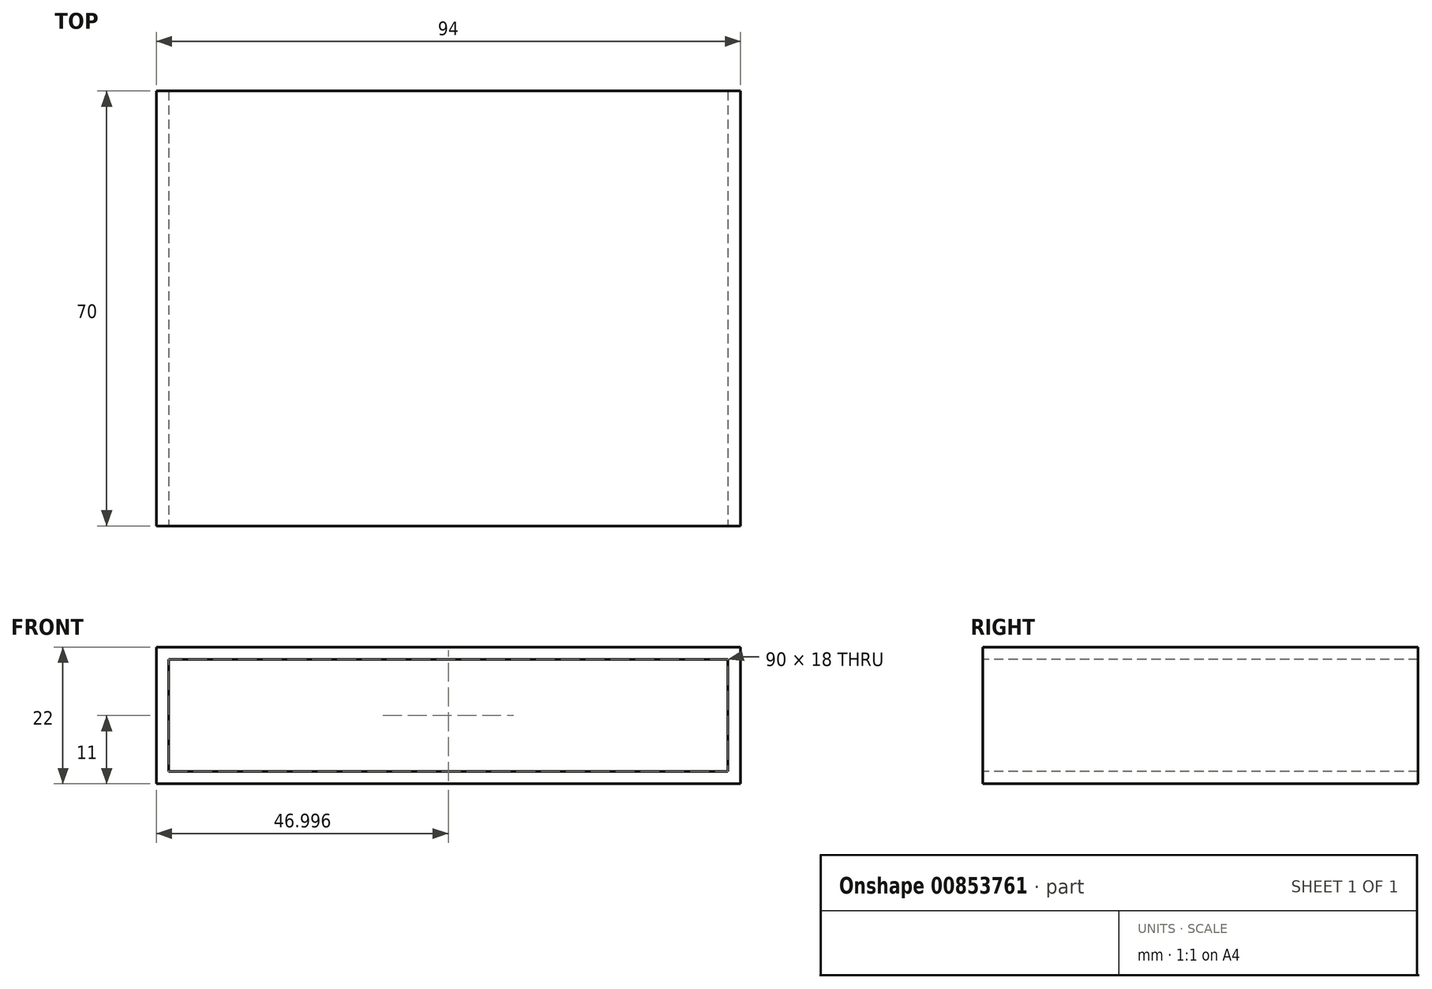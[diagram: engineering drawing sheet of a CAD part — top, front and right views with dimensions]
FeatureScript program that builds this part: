
annotation { "Feature Type Name" : "Feature", "Feature Type Description" : "" }
export const myFeature = defineFeature(function(context is Context, id is Id, definition is map)
    precondition{}
    {
        {
            var Q0;
            Q0=qCreatedBy(makeId("Front.planeOp"),FACE);
            var sketch = newSketch(context, id + "F0", { "sketchPlane" : qUnion([Q0])});
            skLineSegment(sketch, "E0.bottom", {"start": v(-44, 0) * mm, "end": v(50, 0) * mm});
            skLineSegment(sketch, "E0.top", {"start": v(-44, 22) * mm, "end": v(50, 22) * mm});
            skLineSegment(sketch, "E0.left", {"start": v(-44, 0) * mm, "end": v(-44, 22) * mm});
            skLineSegment(sketch, "E0.right", {"start": v(50, 0) * mm, "end": v(50, 22) * mm});
            skLineSegment(sketch, "E1.bottom", {"start": v(-42, 2) * mm, "end": v(48, 2) * mm});
            skLineSegment(sketch, "E1.top", {"start": v(-42, 20) * mm, "end": v(48, 20) * mm});
            skLineSegment(sketch, "E1.left", {"start": v(-42, 2) * mm, "end": v(-42, 20) * mm});
            skLineSegment(sketch, "E1.right", {"start": v(48, 2) * mm, "end": v(48, 20) * mm});
            skSolve(sketch);
        }
        {
            var Q0;
            Q0 = qSketchRegion(id + "F0", true);
            extrude(context, id + "F1", {"entities" : qUnion([Q0]), "endBound" : BoundingType.SYMMETRIC, "oppositeDirection" : true, "depth" : 70 * mm, "offsetDistance" : 25 * mm});
        }
    });
